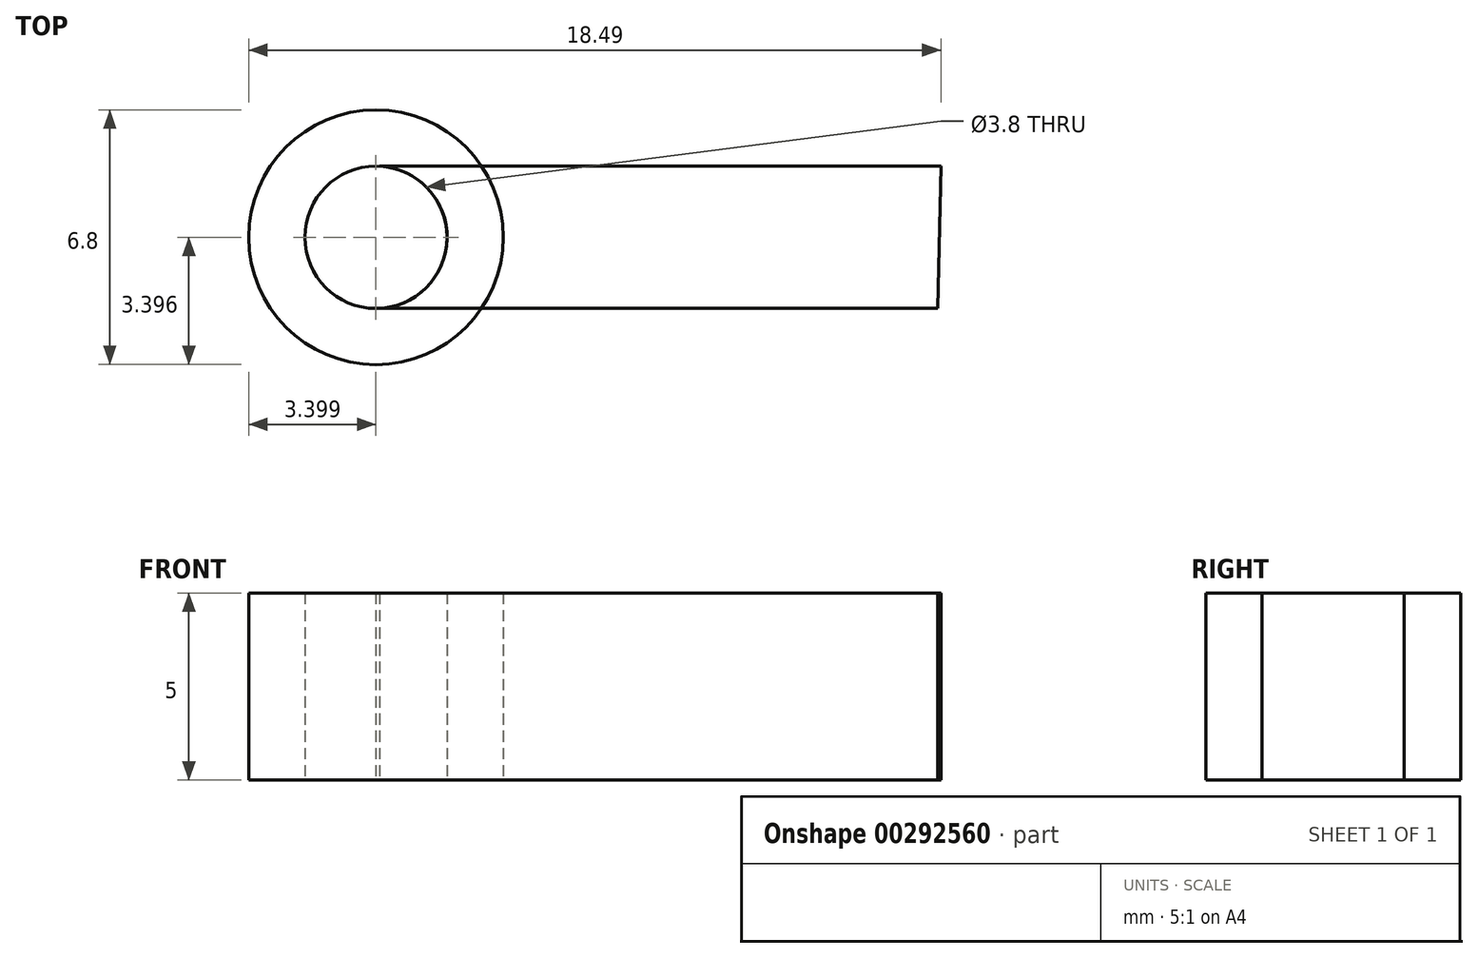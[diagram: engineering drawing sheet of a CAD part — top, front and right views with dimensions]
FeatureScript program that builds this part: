
annotation { "Feature Type Name" : "Feature", "Feature Type Description" : "" }
export const myFeature = defineFeature(function(context is Context, id is Id, definition is map)
    precondition{}
    {
        {
            var Q0;
            Q0=qCreatedBy(makeId("Top.planeOp"),FACE);
            var sketch = newSketch(context, id + "F0", { "sketchPlane" : qUnion([Q0])});
            skCircle(sketch, "E0", {"center": v(1.3, 1.39) * mm, "radius": 1.9 * mm});
            skLineSegment(sketch, "E1", {"start": v(1.39, 3.28) * mm, "end": v(16.39, 3.28) * mm});
            skLineSegment(sketch, "E2", {"start": v(1.3, -0.51) * mm, "end": v(16.3, -0.51) * mm});
            skLineSegment(sketch, "E3", {"start": v(16.39, 3.28) * mm, "end": v(16.3, -0.51) * mm});
            skSolve(sketch);
        }
        {
            var Q0;
            Q0=qCreatedBy(makeId("Top.planeOp"),FACE);
            var sketch = newSketch(context, id + "F1", { "sketchPlane" : qUnion([Q0])});
            skCircle(sketch, "E4.0", {"center": v(1.3, 1.39) * mm, "radius": 3.4 * mm});
            skSolve(sketch);
        }
        {
            var Q0;
            Q0=makeQuery(id+"F1.imprint","IMPRINT",FACE,{"disambiguationData":[TD([[makeQuery(id+"F1.imprint","IMPRINT",EDGE,{"derivedFrom":sQuery(id+"F1.wireOp",EDGE,"E4.0")}),1.0]])]});
            extrude(context, id + "F2", {"entities" : qUnion([Q0]), "depth" : 5 * mm});
        }
        {
            var Q0;
            Q0=makeQuery(id+"F0.imprint","IMPRINT",FACE,{"disambiguationData":[TD([[makeQuery(id+"F0.imprint","IMPRINT",EDGE,{"derivedFrom":sQuery(id+"F0.wireOp",EDGE,"E0")}),1.0]])]});
            extrude(context, id + "F3", {"entities" : qUnion([Q0]), "operationType" : NewBodyOperationType.REMOVE, "depth" : 25 * mm});
        }
        {
            var Q0;
            {var subQ0=sQuery(id+"F0.wireOp",EDGE,"E1");Q0=makeQuery(id+"F0.imprint","IMPRINT",FACE,{"disambiguationData":[TD([[makeQuery(id+"F0.imprint","IMPRINT",EDGE,{"derivedFrom":subQ0}),-1.0]])]});}
            extrude(context, id + "F4", {"entities" : qUnion([Q0]), "depth" : 5 * mm});
        }
    });
